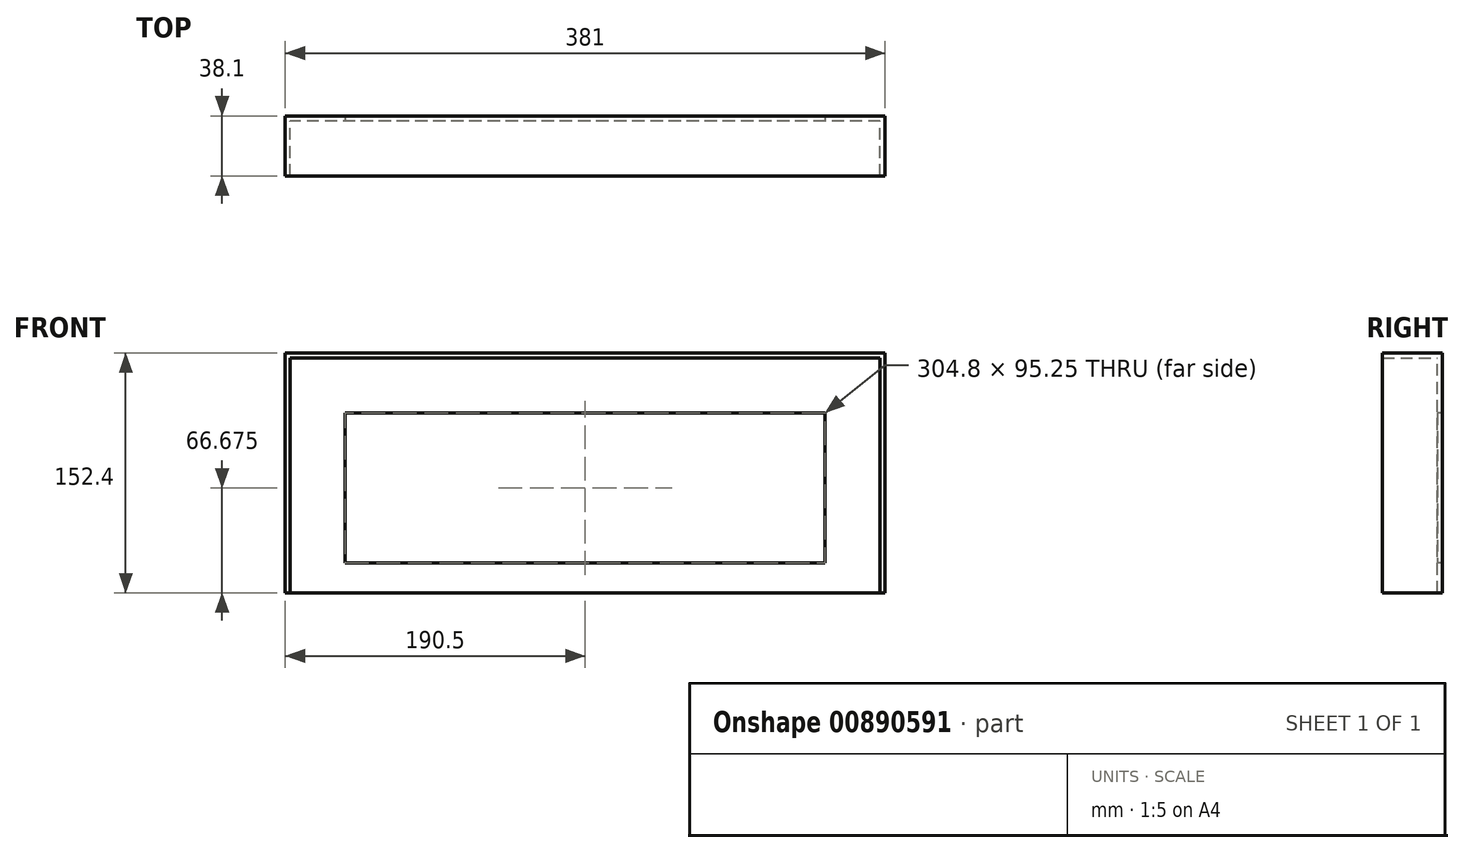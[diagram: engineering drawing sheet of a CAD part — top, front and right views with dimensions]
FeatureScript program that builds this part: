
annotation { "Feature Type Name" : "Feature", "Feature Type Description" : "" }
export const myFeature = defineFeature(function(context is Context, id is Id, definition is map)
    precondition{}
    {
        {
            var Q0;
            Q0=qCreatedBy(makeId("Front.planeOp"),FACE);
            var sketch = newSketch(context, id + "F0", { "sketchPlane" : qUnion([Q0])});
            skLineSegment(sketch, "E0.bottom", {"start": v(190.5, -76.2) * mm, "end": v(-190.5, -76.2) * mm});
            skLineSegment(sketch, "E0.top", {"start": v(190.5, 76.2) * mm, "end": v(-190.5, 76.2) * mm});
            skLineSegment(sketch, "E0.left", {"start": v(190.5, -76.2) * mm, "end": v(190.5, 76.2) * mm});
            skLineSegment(sketch, "E0.right", {"start": v(-190.5, -76.2) * mm, "end": v(-190.5, 76.2) * mm});
            skPoint(sketch, "E0.middle", {"position": v(0, 0) * mm});
            skSolve(sketch);
        }
        {
            var Q0;
            Q0=makeQuery(id+"F0.imprint","IMPRINT",FACE,{"disambiguationData":[TD([[makeQuery(id+"F0.imprint","IMPRINT",EDGE,{"derivedFrom":sQuery(id+"F0.wireOp",EDGE,"E0.bottom")}),-1.0]])]});
            extrude(context, id + "F1", {"entities" : qUnion([Q0]), "depth" : 38.1 * mm, "offsetDistance" : 25.4 * mm});
        }
        {
            var Q0;
            Q0=makeQuery(id+"F1.opExtrude","CAP_FACE",FACE,{"disambiguationData":[OSD([sQuery(id+"F0.wireOp",EDGE,"E0.bottom"),sQuery(id+"F0.wireOp",EDGE,"E0.top"),sQuery(id+"F0.wireOp",EDGE,"E0.left"),sQuery(id+"F0.wireOp",EDGE,"E0.right")])],"isStart":false});
            var Q1;
            Q1=makeQuery(id+"F1.opExtrude","SWEPT_FACE",FACE,{"disambiguationData":[OSD([sQuery(id+"F0.wireOp",EDGE,"E0.bottom")])]});
            shell(context, id + "F2", {"entities" : qUnion([Q0, Q1]), "thickness" : 3.17 * mm});
        }
        {
            var Q0;
            Q0=makeQuery(id+"F2.opShell","OFFSET_FACE",FACE,{"disambiguationData":[OSD([sQuery(id+"F0.wireOp",EDGE,"E0.bottom"),sQuery(id+"F0.wireOp",EDGE,"E0.top"),sQuery(id+"F0.wireOp",EDGE,"E0.left"),sQuery(id+"F0.wireOp",EDGE,"E0.right")])]});
            var sketch = newSketch(context, id + "F3", { "sketchPlane" : qUnion([Q0])});
            skLineSegment(sketch, "E1.bottom", {"start": v(152.4, 38.1) * mm, "end": v(-152.4, 38.1) * mm});
            skLineSegment(sketch, "E1.top", {"start": v(152.4, -57.15) * mm, "end": v(-152.4, -57.15) * mm});
            skLineSegment(sketch, "E1.left", {"start": v(152.4, 38.1) * mm, "end": v(152.4, -57.15) * mm});
            skLineSegment(sketch, "E1.right", {"start": v(-152.4, 38.1) * mm, "end": v(-152.4, -57.15) * mm});
            skPoint(sketch, "E1.middle", {"position": v(0, -9.53) * mm});
            skSolve(sketch);
        }
        {
            var Q0;
            Q0=makeQuery(id+"F3.imprint","IMPRINT",FACE,{"disambiguationData":[TD([[makeQuery(id+"F3.imprint","IMPRINT",EDGE,{"derivedFrom":sQuery(id+"F3.wireOp",EDGE,"E1.bottom")}),1.0]])]});
            extrude(context, id + "F4", {"entities" : qUnion([Q0]), "operationType" : NewBodyOperationType.REMOVE, "oppositeDirection" : true, "depth" : 25.4 * mm, "offsetDistance" : 25.4 * mm});
        }
    });
